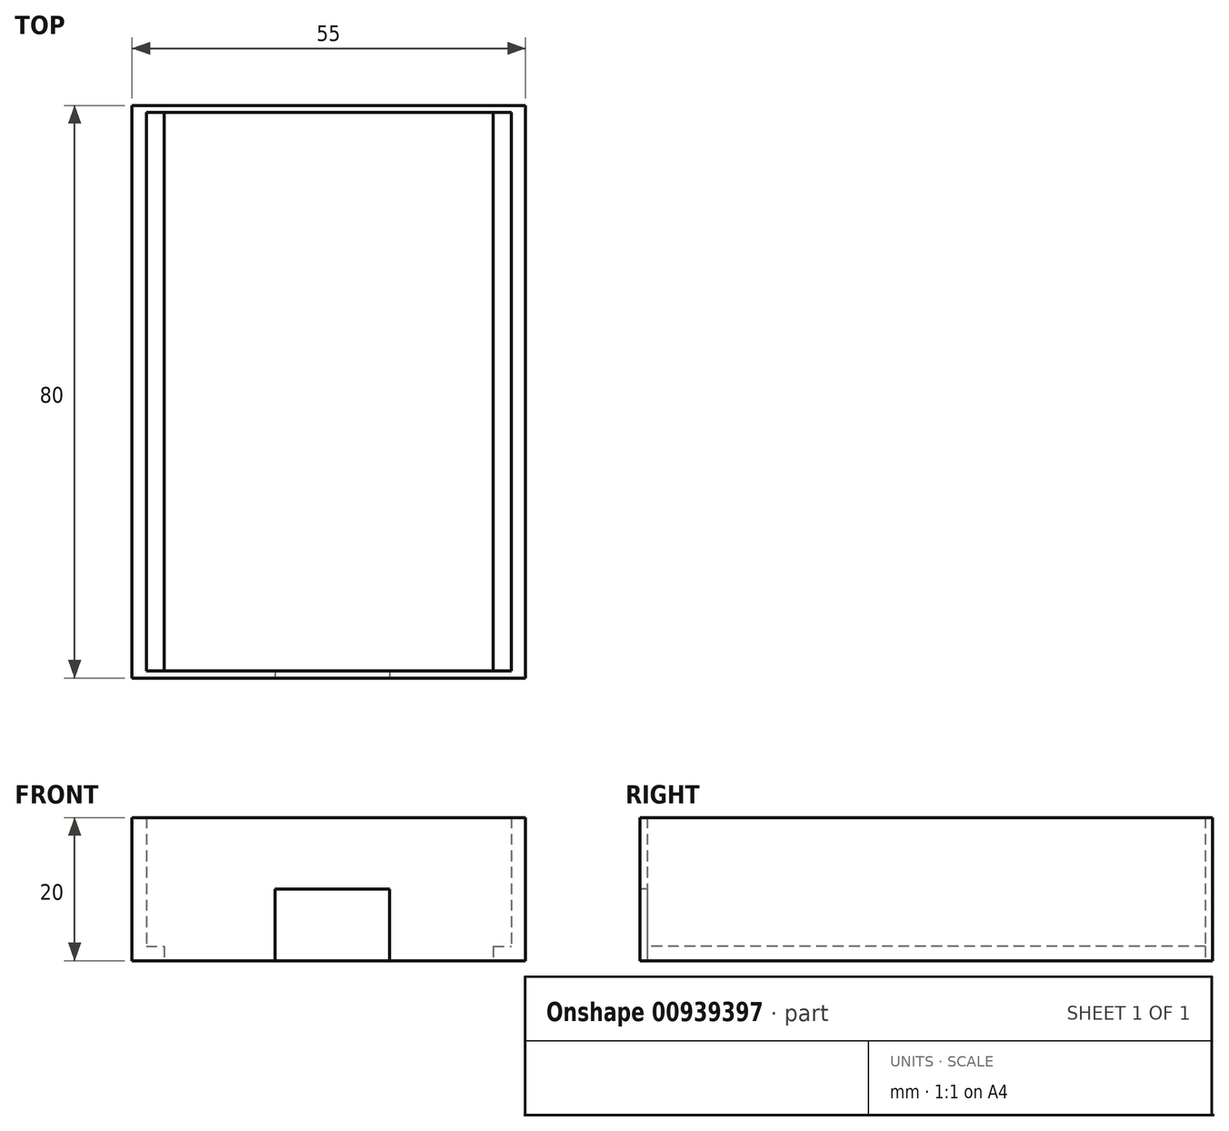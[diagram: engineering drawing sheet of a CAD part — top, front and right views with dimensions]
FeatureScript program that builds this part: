
annotation { "Feature Type Name" : "Feature", "Feature Type Description" : "" }
export const myFeature = defineFeature(function(context is Context, id is Id, definition is map)
    precondition{}
    {
        {
            var Q0;
            Q0=qCreatedBy(makeId("Top.planeOp"),FACE);
            var sketch = newSketch(context, id + "F0", { "sketchPlane" : qUnion([Q0])});
            skLineSegment(sketch, "E0.bottom", {"start": v(23, -35) * mm, "end": v(-23, -35) * mm});
            skLineSegment(sketch, "E0.top", {"start": v(23, 35) * mm, "end": v(-23, 35) * mm});
            skLineSegment(sketch, "E0.left", {"start": v(23, -35) * mm, "end": v(23, 35) * mm});
            skLineSegment(sketch, "E0.right", {"start": v(-23, -35) * mm, "end": v(-23, 35) * mm});
            skPoint(sketch, "E0.middle", {"position": v(0, 0) * mm});
            skLineSegment(sketch, "E1.bottom", {"start": v(27.5, -40) * mm, "end": v(-27.5, -40) * mm});
            skLineSegment(sketch, "E1.top", {"start": v(27.5, 40) * mm, "end": v(-27.5, 40) * mm});
            skLineSegment(sketch, "E1.left", {"start": v(27.5, -40) * mm, "end": v(27.5, 40) * mm});
            skLineSegment(sketch, "E1.right", {"start": v(-27.5, -40) * mm, "end": v(-27.5, 40) * mm});
            skLineSegment(sketch, "E2.bottom", {"start": v(25.5, -39) * mm, "end": v(-25.5, -39) * mm});
            skLineSegment(sketch, "E2.top", {"start": v(25.5, 39) * mm, "end": v(-25.5, 39) * mm});
            skLineSegment(sketch, "E2.left", {"start": v(25.5, -39) * mm, "end": v(25.5, 39) * mm});
            skLineSegment(sketch, "E2.right", {"start": v(-25.5, -39) * mm, "end": v(-25.5, 39) * mm});
            skLineSegment(sketch, "E3", {"start": v(-23, -35) * mm, "end": v(-23, -39) * mm});
            skLineSegment(sketch, "E4", {"start": v(23, -35) * mm, "end": v(23, -39) * mm});
            skLineSegment(sketch, "E5", {"start": v(-23, 35) * mm, "end": v(-23, 39) * mm});
            skLineSegment(sketch, "E6", {"start": v(23, 35) * mm, "end": v(23, 39) * mm});
            skLineSegment(sketch, "E7", {"start": v(-25.5, -39) * mm, "end": v(-7.5, -39) * mm});
            skLineSegment(sketch, "E8", {"start": v(-7.5, -39) * mm, "end": v(8.5, -39) * mm});
            skLineSegment(sketch, "E9", {"start": v(-7.5, -39) * mm, "end": v(-7.5, -40) * mm});
            skLineSegment(sketch, "E10", {"start": v(8.5, -39) * mm, "end": v(8.5, -40) * mm});
            skSolve(sketch);
        }
        {
            var Q0;
            Q0=makeQuery(id+"F0.imprint","IMPRINT",FACE,{"disambiguationData":[TD([[makeQuery(id+"F0.imprint","IMPRINT",EDGE,{"derivedFrom":sQuery(id+"F0.wireOp",EDGE,"E0.right")}),1.0]])]});
            var Q1;
            Q1=makeQuery(id+"F0.imprint","IMPRINT",FACE,{"disambiguationData":[TD([[makeQuery(id+"F0.imprint","IMPRINT",EDGE,{"derivedFrom":sQuery(id+"F0.wireOp",EDGE,"E1.top")}),1.0]])]});
            var Q2;
            Q2=makeQuery(id+"F0.imprint","IMPRINT",FACE,{"disambiguationData":[TD([[makeQuery(id+"F0.imprint","IMPRINT",EDGE,{"derivedFrom":sQuery(id+"F0.wireOp",EDGE,"E0.left")}),-1.0]])]});
            extrude(context, id + "F1", {"entities" : qUnion([Q0, Q1, Q2]), "depth" : 2 * mm, "offsetDistance" : 25 * mm});
        }
        {
            var Q0;
            Q0=makeQuery(id+"F0.imprint","IMPRINT",FACE,{"disambiguationData":[TD([[makeQuery(id+"F0.imprint","IMPRINT",EDGE,{"derivedFrom":sQuery(id+"F0.wireOp",EDGE,"E1.top")}),1.0]])]});
            extrude(context, id + "F2", {"entities" : qUnion([Q0]), "operationType" : NewBodyOperationType.ADD, "depth" : 20 * mm, "offsetDistance" : 25 * mm});
        }
        {
            var Q0;
            {var subQ0=sQuery(id+"F0.wireOp",EDGE,"E9");Q0=makeQuery(id+"F0.imprint","IMPRINT",FACE,{"disambiguationData":[TD([[makeQuery(id+"F0.imprint","IMPRINT",EDGE,{"derivedFrom":subQ0}),1.0]])]});}
            extrude(context, id + "F3", {"entities" : qUnion([Q0]), "operationType" : NewBodyOperationType.ADD, "depth" : 20 * mm, "offsetDistance" : 25 * mm});
        }
        {
            var Q0;
            {var subQ0=sQuery(id+"F0.wireOp",EDGE,"E9");Q0=makeQuery(id+"F0.imprint","IMPRINT",FACE,{"disambiguationData":[TD([[makeQuery(id+"F0.imprint","IMPRINT",EDGE,{"derivedFrom":subQ0}),1.0]])]});}
            extrude(context, id + "F4", {"entities" : qUnion([Q0]), "operationType" : NewBodyOperationType.REMOVE, "depth" : 10 * mm, "offsetDistance" : 25 * mm});
        }
    });
